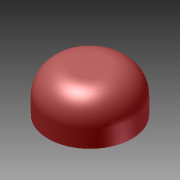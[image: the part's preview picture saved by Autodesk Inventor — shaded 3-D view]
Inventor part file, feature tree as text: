
AUTODESK INVENTOR PART (.ipt)
format: ipt  version: 2011 SP1 (Build 150282100, 282)  size: 107,520 bytes
history: native  units: in
note: dims shown in document units (in); Inventor stores cm internally (conversion verified against a paired STEP export)
features: other x7, revolve x1, sketch x1
ambient origin geometry x8: Origin, YZ Plane, XZ Plane, XY Plane, X Axis, Y Axis, Z Axis, Center Point
bodies: Solid1 (feature_tree)
feature tree (9):
  revolve  "Revolution1"  [1 undecoded]
  other  "full_led_to_act_XY"
  other  "full_led_to_act_YZ"
  other  "full_led_to_act_ZX"
  other  "full_led_to_act_X"
  other  "full_led_to_act_Y"
  other  "full_led_to_act_Z"
  other  "full_led_to_act_Center"
  sketch  "Sketch_1"  dims[d0=360.0deg]
note: 1 required parameter value undecoded (feature->parameter linkage not recoverable at this tier; creation-order binding heuristic only, values carry confidence <= 0.55)
